# Revit family: PortalsConnect_88H & 94H_US
name_source: partatom
category: Furniture Systems
units: mm (PartAtom-declared; Revit-internal decimal feet)

## family parameters
Always vertical = Yes
Cut with Voids When Loaded = No
Enable Cutting in Views = No
Part Type = Normal
Room Calculation Point = No
Round Connector Dimension = Use Diameter
Shared = No
Work Plane-Based = No

## types (1)
- PortalsConnect_88H & 94H_US
    Accessories = <By Category>
    Chain = <By Category>
    Clade Roof = <By Category>
    Clade Side = <By Category>
    Dash Board = <By Category>
    Default Elevation = 0 "
    Description = Portals Connect
,  1800mmX1200X 2235H
    Door Frame = <By Category>
    Door Glass = <By Category>
    Door Pull = <By Category>
    Fan = <By Category>
    Fan Frame = <By Category>
    Feet = <By Category>
    Frame Rubber = <By Category>
    Inner Clade = <By Category>
    Leg = <By Category>
    Lower Back Clade = <By Category>
    Lower Side Clade = <By Category>
    Manufacturer = Spacestor
    Model = PTC-DDA
    Monitor = <By Category>
    Monitor Stand = <By Category>
    Receptacle = <By Category>
    Roof Upholstery = <By Category>
    Side Rubber = <By Category>
    Sportlight = <By Category>
    Support = <By Category>
    Support Pad = <By Category>
    URL = https://spacestor.com
    Upholstery Frame = <By Category>
    Upper Side Clade = <By Category>
    Uppor Back Clade = <By Category>
    Wire = <By Category>
    Worksurface = <By Category>

## geometry (parser evidence)
native form markers: Sweep x2
no freeform markers — native parametric forms only
